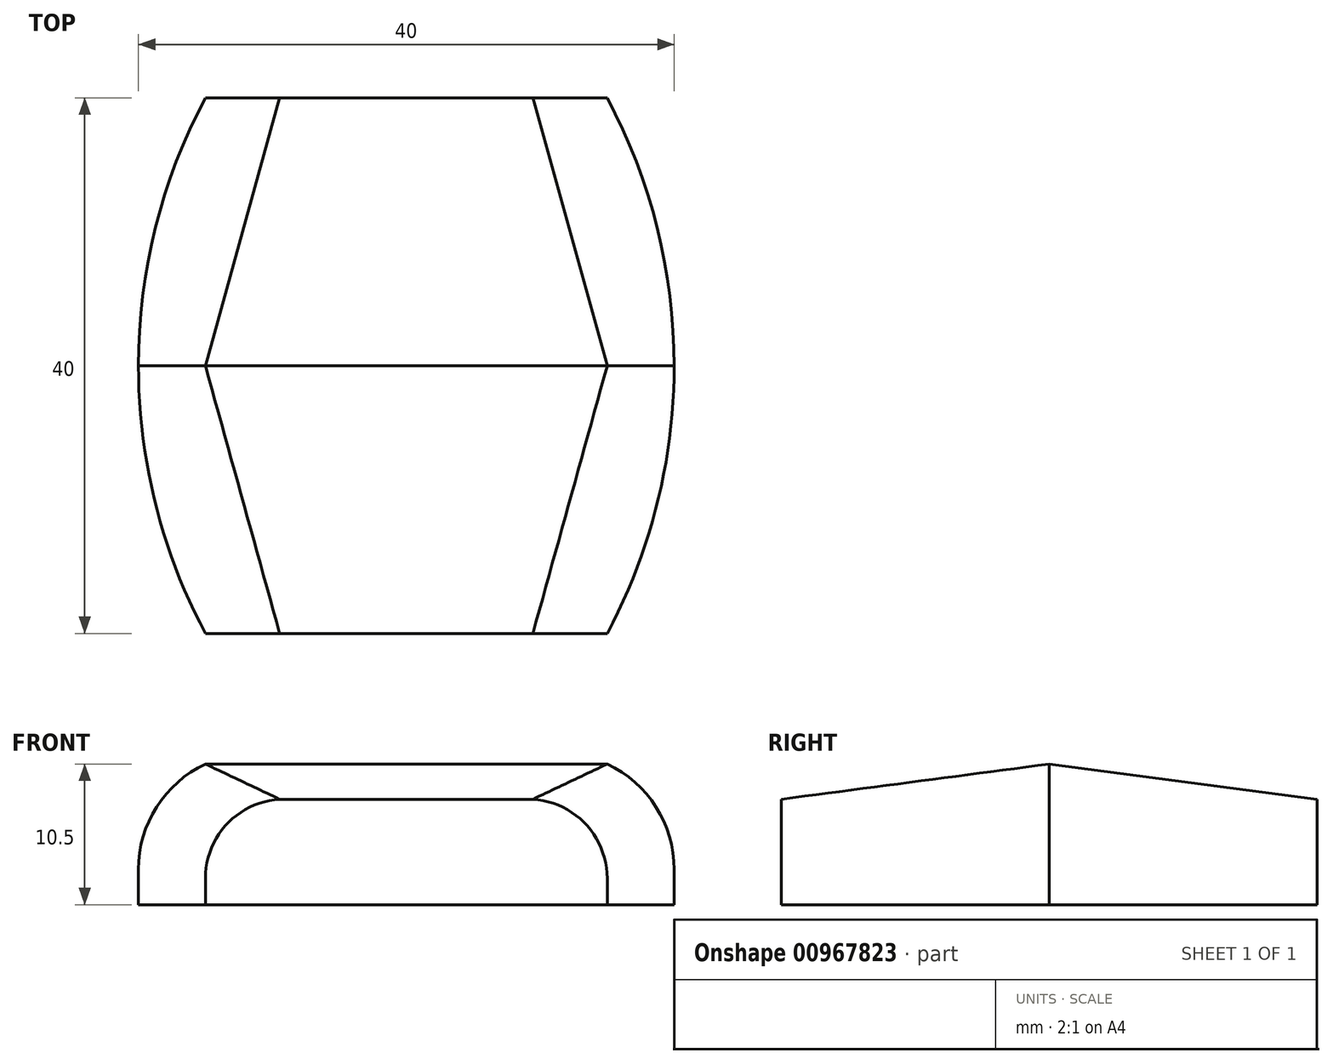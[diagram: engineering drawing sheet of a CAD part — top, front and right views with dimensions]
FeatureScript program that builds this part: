
annotation { "Feature Type Name" : "Feature", "Feature Type Description" : "" }
export const myFeature = defineFeature(function(context is Context, id is Id, definition is map)
    precondition{}
    {
        {
            assignVariable(context, id + "F0", {"name" : "Width", "anyValue" : 40 * mm});
        }
        {
            var Q0;
            Q0=qCreatedBy(makeId("Front.planeOp"),FACE);
            var sketch = newSketch(context, id + "F1", { "sketchPlane" : qUnion([Q0])});
            skLineSegment(sketch, "E0.bottom", {"start": v(20, 5.25) * mm, "end": v(-20, 5.25) * mm});
            skLineSegment(sketch, "E0.top", {"start": v(20, -5.25) * mm, "end": v(-20, -5.25) * mm});
            skLineSegment(sketch, "E0.left", {"start": v(20, 5.25) * mm, "end": v(20, 0) * mm});
            skLineSegment(sketch, "E0.right", {"start": v(-20, 5.25) * mm, "end": v(-20, 0) * mm});
            skPoint(sketch, "E0.middle", {"position": v(0, 0) * mm});
            skPoint(sketch, "E1.snap10", {"position": v(0, 5.25) * mm});
            skPoint(sketch, "E2", {"position": v(20, 0) * mm});
            skLineSegment(sketch, "E3", {"start": v(20, 0) * mm, "end": v(20, -2.63) * mm});
            skLineSegment(sketch, "E4", {"start": v(20, -2.63) * mm, "end": v(20, -5.25) * mm});
            skLineSegment(sketch, "E5", {"start": v(-20, 0) * mm, "end": v(-20, -2.63) * mm});
            skLineSegment(sketch, "E6", {"start": v(-20, -2.63) * mm, "end": v(-20, -5.25) * mm});
            skLineSegment(sketch, "E7", {"start": v(0, 5.25) * mm, "end": v(-15, 5.25) * mm});
            skLineSegment(sketch, "E8", {"start": v(0, 5.25) * mm, "end": v(15, 5.25) * mm});
            skArc(sketch, "E9", {"start": v(20, -2.63) * mm, "mid": v(18.64, 2.04) * mm, "end": v(15, 5.25) * mm});
            skArc(sketch, "E10.MirrorCS", {"start": v(-20, -2.63) * mm, "mid": v(-18.64, 2.04) * mm, "end": v(-15, 5.25) * mm});
            skSolve(sketch);
        }
        {
            var Q0;
            Q0=qCreatedBy(makeId("Front.planeOp"),FACE);
            cPlane(context, id + "F2", {"entities" : qUnion([Q0]), "cplaneType" : CPlaneType.OFFSET, "offset" : getVariable(context, 'Width') / 2, "oppositeDirection" : true, "width" : 150 * mm, "height" : 150 * mm});
        }
        {
            var Q0;
            Q0=qCreatedBy(id+"F2.planeOp",FACE);
            var sketch = newSketch(context, id + "F3", { "sketchPlane" : qUnion([Q0])});
            skLineSegment(sketch, "E11.bottom", {"start": v(15, 2.62) * mm, "end": v(-15, 2.62) * mm});
            skLineSegment(sketch, "E11.top", {"start": v(15, -5.25) * mm, "end": v(-15, -5.25) * mm});
            skLineSegment(sketch, "E11.left", {"start": v(15, 2.63) * mm, "end": v(15, -1.31) * mm});
            skLineSegment(sketch, "E11.right", {"start": v(-15, 2.62) * mm, "end": v(-15, -1.31) * mm});
            skPoint(sketch, "E11.middle", {"position": v(0, -1.31) * mm});
            skPoint(sketch, "E12.snap10", {"position": v(0, 2.62) * mm});
            skPoint(sketch, "E13", {"position": v(15, -1.31) * mm});
            skLineSegment(sketch, "E14", {"start": v(15, -1.31) * mm, "end": v(15, -3.28) * mm});
            skLineSegment(sketch, "E15", {"start": v(15, -3.28) * mm, "end": v(15, -5.25) * mm});
            skLineSegment(sketch, "E16", {"start": v(-15, -1.31) * mm, "end": v(-15, -3.28) * mm});
            skLineSegment(sketch, "E17", {"start": v(-15, -3.28) * mm, "end": v(-15, -5.25) * mm});
            skLineSegment(sketch, "E18", {"start": v(0, 2.62) * mm, "end": v(-11.25, 2.62) * mm});
            skLineSegment(sketch, "E19", {"start": v(0, 2.62) * mm, "end": v(9.45, 2.62) * mm});
            skArc(sketch, "E20", {"start": v(15, -3.28) * mm, "mid": v(13.4, 0.77) * mm, "end": v(9.45, 2.62) * mm});
            skArc(sketch, "E21.MirrorCS", {"start": v(-15, -3.28) * mm, "mid": v(-13.4, 0.77) * mm, "end": v(-9.45, 2.62) * mm});
            skSolve(sketch);
        }
        {
            var Q0;
            Q0=sQuery(id+"F3.wireOp",EDGE,"E11.top");
            var Q1;
            Q1=sQuery(id+"F1.wireOp",EDGE,"E0.top");
            cPlane(context, id + "F4", {"entities" : qUnion([Q0, Q1]), "cplaneType" : CPlaneType.LINE_ANGLE, "offset" : 25 * mm, "angle" : 0 * degree, "width" : 150 * mm, "height" : 150 * mm});
        }
        {
            var Q0;
            Q0=qCreatedBy(id+"F4.planeOp",FACE);
            var sketch = newSketch(context, id + "F5", { "sketchPlane" : qUnion([Q0])});
            skArc(sketch, "E22", {"start": v(20, 0) * mm, "mid": v(18.73, 10.3) * mm, "end": v(15, 20) * mm});
            skArc(sketch, "E23.MirrorCS", {"start": v(-20, 0) * mm, "mid": v(-18.73, 10.3) * mm, "end": v(-15, 20) * mm});
            skSolve(sketch);
        }
        {
            var Q0;
            Q0=makeQuery(id+"F1.imprint","IMPRINT",FACE,{"disambiguationData":[TD([[makeQuery(id+"F1.imprint","IMPRINT",EDGE,{"derivedFrom":sQuery(id+"F1.wireOp",EDGE,"E0.top")}),-1.0]])]});
            var Q1;
            Q1=makeQuery(id+"F3.imprint","IMPRINT",FACE,{"disambiguationData":[TD([[makeQuery(id+"F3.imprint","IMPRINT",EDGE,{"derivedFrom":sQuery(id+"F3.wireOp",EDGE,"E11.top")}),-1.0]])]});
            var Q2;
            Q2=sQuery(id+"F5.wireOp",EDGE,"E22");
            var Q3;
            Q3=sQuery(id+"F5.wireOp",EDGE,"E23.MirrorCS");
            loft(context, id + "F6", {"addGuides" : true, "sheetProfilesArray" : [{ "sheetProfileEntities" : qUnion([Q0]) }, { "sheetProfileEntities" : qUnion([Q1]) }], "guidesArray" : [{ "guideEntities" : qUnion([Q2]), "guideDerivativeType" : LoftGuideDerivativeType.DEFAULT, "guideDerivativeMagnitude" : 1 }, { "guideEntities" : qUnion([Q3]), "guideDerivativeType" : LoftGuideDerivativeType.DEFAULT, "guideDerivativeMagnitude" : 1 }]});
        }
        {
            var Q0;
            Q0=makeQuery(id+"F6.opLoft","SWEPT_BODY",BODY,{"disambiguationData":[OSD([makeQuery(id+"F1.imprint","IMPRINT",FACE,{"disambiguationData":[TD([[makeQuery(id+"F1.imprint","IMPRINT",EDGE,{"derivedFrom":sQuery(id+"F1.wireOp",EDGE,"E0.top")}),-1.0]])]}),makeQuery(id+"F3.imprint","IMPRINT",FACE,{"disambiguationData":[TD([[makeQuery(id+"F3.imprint","IMPRINT",EDGE,{"derivedFrom":sQuery(id+"F3.wireOp",EDGE,"E11.top")}),-1.0]])]}),sQuery(id+"F5.wireOp",EDGE,"E22"),sQuery(id+"F5.wireOp",EDGE,"E23.MirrorCS")])]});
            var Q1;
            Q1=qCreatedBy(makeId("Front.planeOp"),FACE);
            mirror(context, id + "F7", {"operationType" : NewBodyOperationType.ADD, "entities" : qUnion([Q0]), "mirrorPlane" : qUnion([Q1])});
        }
    });
